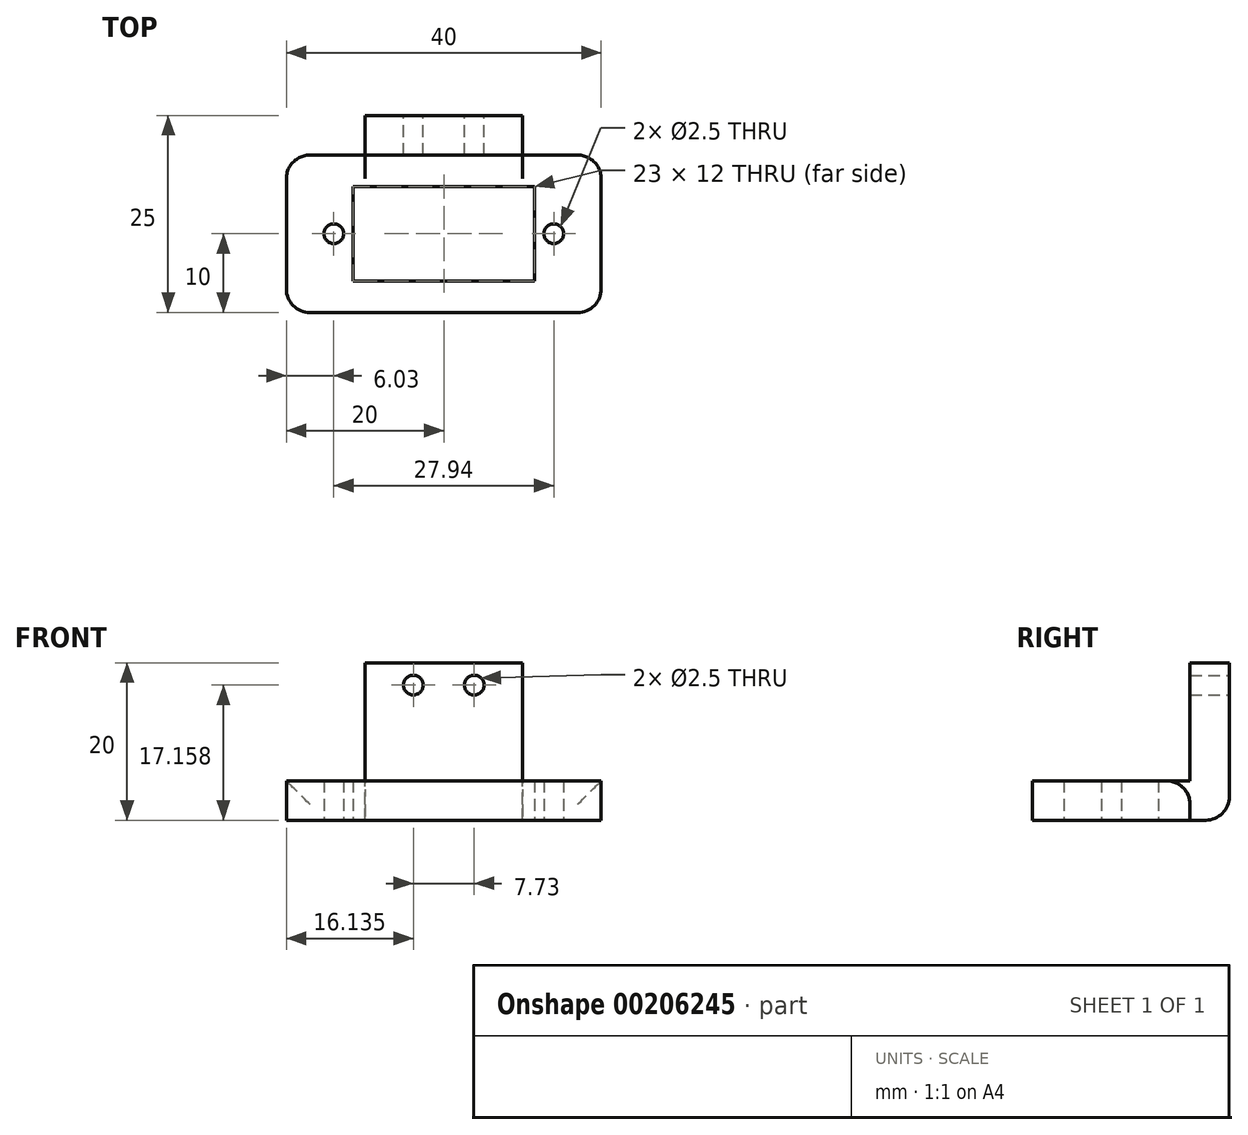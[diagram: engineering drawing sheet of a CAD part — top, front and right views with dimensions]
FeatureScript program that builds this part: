
annotation { "Feature Type Name" : "Feature", "Feature Type Description" : "" }
export const myFeature = defineFeature(function(context is Context, id is Id, definition is map)
    precondition{}
    {
        {
            var Q0;
            Q0=qCreatedBy(makeId("Top.planeOp"),FACE);
            var sketch = newSketch(context, id + "F0", { "sketchPlane" : qUnion([Q0])});
            skLineSegment(sketch, "E0.bottom", {"start": v(-20, 10) * mm, "end": v(-10, 10) * mm});
            skLineSegment(sketch, "E0.top", {"start": v(-20, -10) * mm, "end": v(20, -10) * mm});
            skLineSegment(sketch, "E0.left", {"start": v(-20, 10) * mm, "end": v(-20, -10) * mm});
            skLineSegment(sketch, "E0.right", {"start": v(20, 10) * mm, "end": v(20, -10) * mm});
            skPoint(sketch, "E0.middle", {"position": v(0, 0) * mm});
            skLineSegment(sketch, "E1.bottom", {"start": v(-11.5, 6) * mm, "end": v(11.5, 6) * mm});
            skLineSegment(sketch, "E1.top", {"start": v(-11.5, -6) * mm, "end": v(11.5, -6) * mm});
            skLineSegment(sketch, "E1.left", {"start": v(-11.5, 6) * mm, "end": v(-11.5, -6) * mm});
            skLineSegment(sketch, "E1.right", {"start": v(11.5, 6) * mm, "end": v(11.5, -6) * mm});
            skPoint(sketch, "E2.endSnap0", {"position": v(0, 10) * mm});
            skLineSegment(sketch, "E3", {"start": v(0, 15) * mm, "end": v(-10, 15) * mm});
            skLineSegment(sketch, "E4", {"start": v(-10, 15) * mm, "end": v(-10, 10) * mm});
            skLineSegment(sketch, "E5", {"start": v(0, 15) * mm, "end": v(10, 15) * mm});
            skLineSegment(sketch, "E6", {"start": v(10, 15) * mm, "end": v(10, 10) * mm});
            skPoint(sketch, "E2.start.orphan", {"position": v(0, 10) * mm});
            skLineSegment(sketch, "E7.trimOffspring", {"start": v(10, 10) * mm, "end": v(20, 10) * mm});
            skLineSegment(sketch, "E8", {"start": v(0, 0) * mm, "end": v(13.97, 0) * mm, "construction": true});
            skPoint(sketch, "E8.endSnap0", {"position": v(11.5, 0) * mm});
            skLineSegment(sketch, "E9", {"start": v(0, 0) * mm, "end": v(-13.97, 0) * mm, "construction": true});
            skCircle(sketch, "E10", {"center": v(13.97, 0) * mm, "radius": 1.25 * mm});
            skCircle(sketch, "E11", {"center": v(-13.97, 0) * mm, "radius": 1.25 * mm});
            skLineSegment(sketch, "E12", {"start": v(-10, 10) * mm, "end": v(10, 10) * mm});
            skSolve(sketch);
        }
        {
            var Q0;
            Q0=makeQuery(id+"F0.imprint","IMPRINT",FACE,{"disambiguationData":[TD([[makeQuery(id+"F0.imprint","IMPRINT",EDGE,{"derivedFrom":sQuery(id+"F0.wireOp",EDGE,"E3")}),1.0]])]});
            extrude(context, id + "F1", {"entities" : qUnion([Q0]), "depth" : 20 * mm});
        }
        {
            var Q0;
            Q0=makeQuery(id+"F0.imprint","IMPRINT",FACE,{"disambiguationData":[TD([[makeQuery(id+"F0.imprint","IMPRINT",EDGE,{"derivedFrom":sQuery(id+"F0.wireOp",EDGE,"E0.bottom")}),-1.0]])]});
            extrude(context, id + "F2", {"entities" : qUnion([Q0]), "operationType" : NewBodyOperationType.ADD, "depth" : 5 * mm});
        }
        {
            var Q0;
            Q0=makeQuery(id+"F1.opExtrude","SWEPT_FACE",FACE,{"disambiguationData":[OSD([sQuery(id+"F0.wireOp",EDGE,"E3"),sQuery(id+"F0.wireOp",EDGE,"E5")])]});
            var sketch = newSketch(context, id + "F3", { "sketchPlane" : qUnion([Q0])});
            skLineSegment(sketch, "E13", {"start": v(0, 17.16) * mm, "end": v(-3.87, 17.16) * mm, "construction": true});
            skLineSegment(sketch, "E14", {"start": v(0, 17.16) * mm, "end": v(3.86, 17.16) * mm, "construction": true});
            skCircle(sketch, "E15", {"center": v(-3.87, 17.16) * mm, "radius": 1.25 * mm});
            skCircle(sketch, "E16", {"center": v(3.86, 17.16) * mm, "radius": 1.25 * mm});
            skSolve(sketch);
        }
        {
            var Q0;
            Q0=makeQuery(id+"F3.imprint","IMPRINT",FACE,{"disambiguationData":[TD([[makeQuery(id+"F3.imprint","IMPRINT",EDGE,{"derivedFrom":sQuery(id+"F3.wireOp",EDGE,"E16")}),1.0]])]});
            var Q1;
            Q1=makeQuery(id+"F3.imprint","IMPRINT",FACE,{"disambiguationData":[TD([[makeQuery(id+"F3.imprint","IMPRINT",EDGE,{"derivedFrom":sQuery(id+"F3.wireOp",EDGE,"E15")}),1.0]])]});
            extrude(context, id + "F4", {"entities" : qUnion([Q0, Q1]), "operationType" : NewBodyOperationType.REMOVE, "oppositeDirection" : true, "depth" : 5 * mm});
        }
        {
            var Q0;
            Q0=makeQuery(id+"F2.opExtrude","SWEPT_EDGE",EDGE,{"disambiguationData":[OSD([sQuery(id+"F0.wireOp",EDGE,"E0.bottom"),sQuery(id+"F0.wireOp",EDGE,"E0.left")])]});
            var Q1;
            Q1=makeQuery(id+"F1.opExtrude","CAP_EDGE",EDGE,{"disambiguationData":[OSD([sQuery(id+"F0.wireOp",EDGE,"E3"),sQuery(id+"F0.wireOp",EDGE,"E5")])],"isStart":true});
            var Q2;
            Q2=makeQuery(id+"F2.opExtrude","SWEPT_EDGE",EDGE,{"disambiguationData":[OSD([sQuery(id+"F0.wireOp",EDGE,"E0.right"),sQuery(id+"F0.wireOp",EDGE,"E7.trimOffspring")])]});
            var Q3;
            Q3=makeQuery(id+"F2.opExtrude","SWEPT_EDGE",EDGE,{"disambiguationData":[OSD([sQuery(id+"F0.wireOp",EDGE,"E0.top"),sQuery(id+"F0.wireOp",EDGE,"E0.right")])]});
            var Q4;
            Q4=makeQuery(id+"F2.opExtrude","SWEPT_EDGE",EDGE,{"disambiguationData":[OSD([sQuery(id+"F0.wireOp",EDGE,"E0.top"),sQuery(id+"F0.wireOp",EDGE,"E0.left")])]});
            var Q5;
            {var subQ0=sQuery(id+"F0.wireOp",EDGE,"E12");var subQ1=sQuery(id+"F0.wireOp",EDGE,"E7.trimOffspring");var subQ2=sQuery(id+"F0.wireOp",EDGE,"E0.bottom");Q5=makeQuery(id+"F2.boolean.opBoolean","SPLIT",EDGE,{"disambiguationData":[topologyDisambiguationEdgeConnected([makeQuery(id+"F1.opExtrude","SWEPT_FACE",FACE,{"disambiguationData":[OSD([subQ0])]}),makeQuery(id+"F2.opExtrude","CAP_FACE",FACE,{"disambiguationData":[OSD([subQ2,sQuery(id+"F0.wireOp",EDGE,"E0.top"),sQuery(id+"F0.wireOp",EDGE,"E0.left"),sQuery(id+"F0.wireOp",EDGE,"E0.right"),sQuery(id+"F0.wireOp",EDGE,"E1.bottom"),sQuery(id+"F0.wireOp",EDGE,"E1.top"),sQuery(id+"F0.wireOp",EDGE,"E1.left"),sQuery(id+"F0.wireOp",EDGE,"E1.right"),subQ1,sQuery(id+"F0.wireOp",EDGE,"E10"),sQuery(id+"F0.wireOp",EDGE,"E11"),subQ0])],"isStart":false})])],"derivedFrom":makeQuery(id+"F2.opExtrude","CAP_EDGE",EDGE,{"disambiguationData":[OSD([subQ2,subQ1,subQ0])],"isStart":false})});}
            fillet(context, id + "F5", {"entities" : qUnion([Q0, Q1, Q2, Q3, Q4, Q5]), "radius" : 3 * mm, "tangentPropagation" : true, "allowEdgeOverflow" : false});
        }
    });
